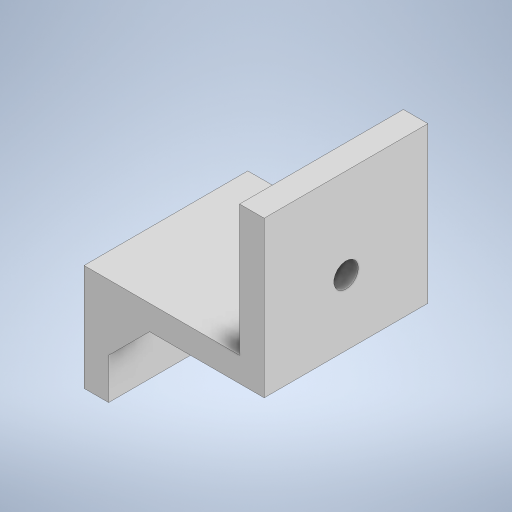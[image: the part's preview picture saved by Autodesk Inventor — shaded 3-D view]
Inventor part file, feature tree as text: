
AUTODESK INVENTOR PART (.ipt)
format: ipt  version: 2023 (Build 270158000, 158)  size: 271,360 bytes
history: native  units: in
note: dims shown in document units (in); Inventor stores cm internally (conversion verified against a paired STEP export)
features: extrude x7, sketch x7
ambient origin geometry x8: Origin, YZ Plane, XZ Plane, XY Plane, X Axis, Y Axis, Z Axis, Center Point
bodies: Solid1 (feature_tree)
feature tree (14):
  extrude  "Extrusion1"  Depth=0.748in
  extrude  "Extrusion4"  Depth=0.1181in
  extrude  "Extrusion5"  Depth=0.7874in TaperAngle=0.0deg
  extrude  "Extrusion6"  Depth=0.1181in
  extrude  "Extrusion7"  Depth=0.7874in TaperAngle=0.0deg
  extrude  "Extrusion8"  Depth=0.3937in
  extrude  "Extrusion9"  TaperAngle=0.0deg  [1 undecoded]
  sketch  "Sketch1"  dims[d0=0.8661in d1=0.748in]
  sketch  "Sketch4"  dims[d2=0.1181in d3=0.1181in]
  sketch  "Sketch5"  dims[d4=0.1181in d5=0.7874in d6=0.0in]
  sketch  "Sketch6"  dims[d15=0.0in d16=0.0in d17=0.1181in]
  sketch  "Sketch7"  dims[d18=0.3937in d19=0.7874in d20=0.0in]
  sketch  "Sketch8"  dims[d21=0.1969in d22=0.3937in]
  sketch  "Sketch9"  dims[d23=0.1969in d24=0.0in d25=0.0in d26=0.1969in d27=0.1969in d28=0.1575in d29=0.0in d30=0.1969in d31=0.1969in d32=0.1575in d33=0.0in d34=0.3937in d35=0.1969in d36=0.1181in d37=0.0in d38=0.0in]
note: 1 required parameter value undecoded (feature->parameter linkage not recoverable at this tier; creation-order binding heuristic only, values carry confidence <= 0.55)
